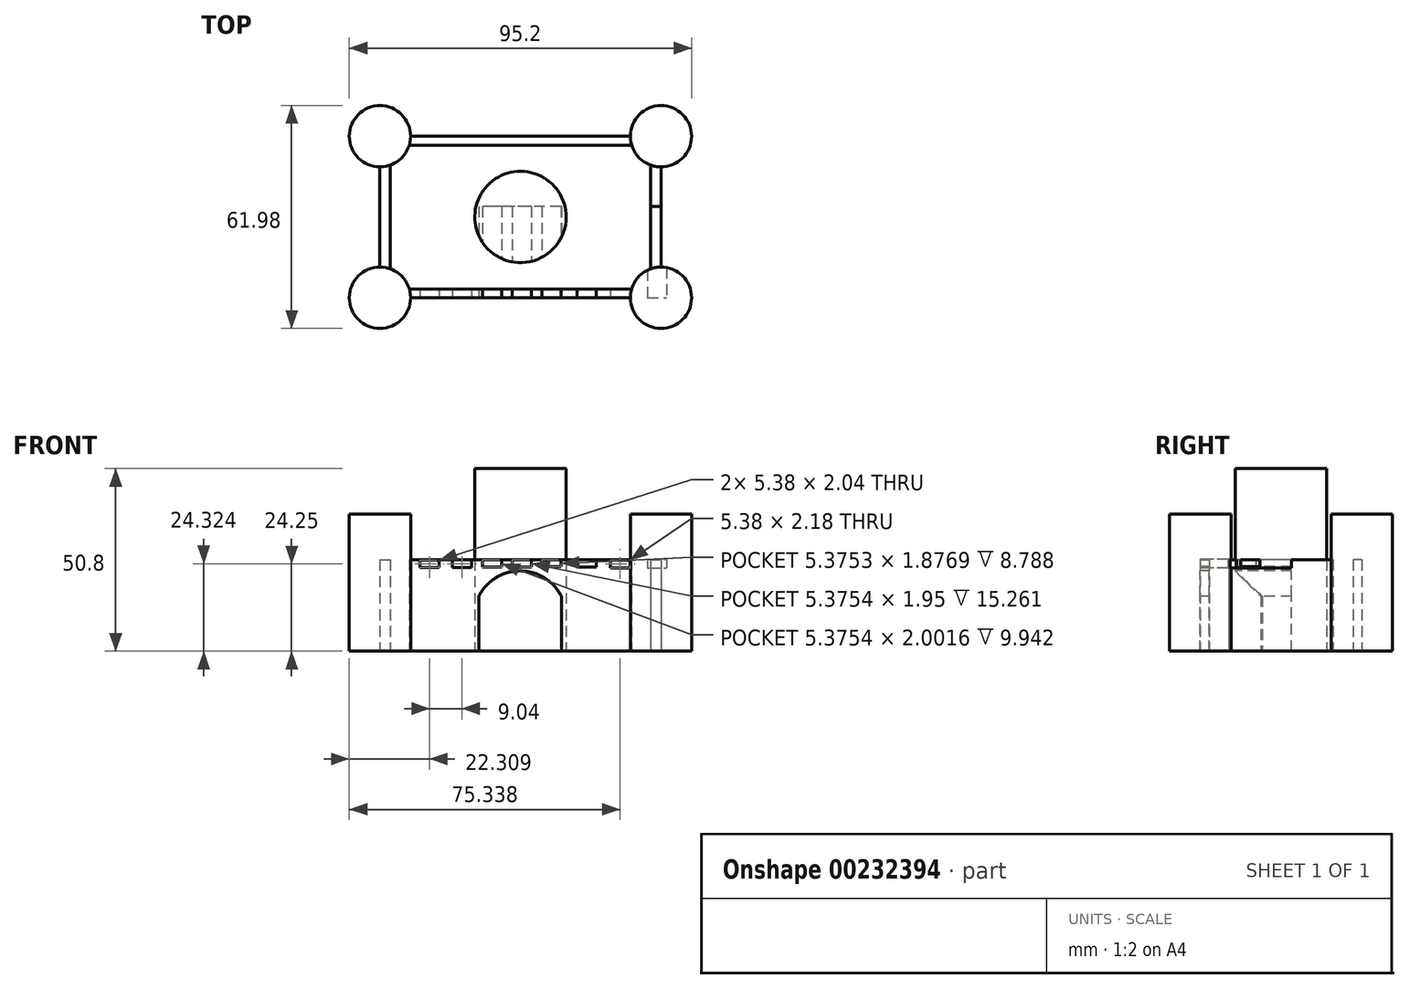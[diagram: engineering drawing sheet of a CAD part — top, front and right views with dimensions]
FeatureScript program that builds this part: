
annotation { "Feature Type Name" : "Feature", "Feature Type Description" : "" }
export const myFeature = defineFeature(function(context is Context, id is Id, definition is map)
    precondition{}
    {
        {
            var Q0;
            Q0=qCreatedBy(makeId("Top.planeOp"),FACE);
            var sketch = newSketch(context, id + "F0", { "sketchPlane" : qUnion([Q0])});
            skLineSegment(sketch, "E0.bottom", {"start": v(30.54, 22.46) * mm, "end": v(-30.54, 22.46) * mm});
            skLineSegment(sketch, "E0.top", {"start": v(30.54, -22.46) * mm, "end": v(-30.54, -22.46) * mm});
            skLineSegment(sketch, "E0.left", {"start": v(39.07, 13.93) * mm, "end": v(39.07, -13.93) * mm});
            skLineSegment(sketch, "E0.right", {"start": v(-39.07, 13.93) * mm, "end": v(-39.07, -13.93) * mm});
            skPoint(sketch, "E0.middle", {"position": v(0, 0) * mm});
            skCircle(sketch, "E1", {"center": v(0, 0) * mm, "radius": 12.7 * mm});
            skCircle(sketch, "E2", {"center": v(-39.07, 22.46) * mm, "radius": 8.53 * mm});
            skCircle(sketch, "E3", {"center": v(39.07, 22.46) * mm, "radius": 8.53 * mm});
            skCircle(sketch, "E4", {"center": v(39.07, -22.46) * mm, "radius": 8.53 * mm});
            skCircle(sketch, "E5", {"center": v(-39.07, -22.46) * mm, "radius": 8.53 * mm});
            skLineSegment(sketch, "E6.bottom", {"start": v(30.9, 20) * mm, "end": v(-30.9, 20) * mm});
            skLineSegment(sketch, "E6.top", {"start": v(30.9, -20) * mm, "end": v(-30.9, -20) * mm});
            skLineSegment(sketch, "E6.left", {"start": v(36.15, 14.45) * mm, "end": v(36.15, -14.45) * mm});
            skLineSegment(sketch, "E6.right", {"start": v(-36.15, 14.45) * mm, "end": v(-36.15, -14.45) * mm});
            skPoint(sketch, "E7.orphan", {"position": v(36.15, 20) * mm});
            skPoint(sketch, "E8.orphan", {"position": v(36.15, -20) * mm});
            skPoint(sketch, "E9.orphan", {"position": v(-36.15, -20) * mm});
            skPoint(sketch, "E10.orphan", {"position": v(-36.15, 20) * mm});
            skSolve(sketch);
        }
        {
            var Q0;
            {var subQ0=sQuery(id+"F0.wireOp",EDGE,"E0.bottom");Q0=makeQuery(id+"F0.imprint","IMPRINT",FACE,{"disambiguationData":[TD([[makeQuery(id+"F0.imprint","IMPRINT",EDGE,{"derivedFrom":subQ0}),1.0]])]});}
            var Q1;
            {var subQ0=sQuery(id+"F0.wireOp",EDGE,"E0.right");Q1=makeQuery(id+"F0.imprint","IMPRINT",FACE,{"disambiguationData":[TD([[makeQuery(id+"F0.imprint","IMPRINT",EDGE,{"derivedFrom":subQ0}),1.0]])]});}
            var Q2;
            {var subQ0=sQuery(id+"F0.wireOp",EDGE,"E0.top");Q2=makeQuery(id+"F0.imprint","IMPRINT",FACE,{"disambiguationData":[TD([[makeQuery(id+"F0.imprint","IMPRINT",EDGE,{"derivedFrom":subQ0}),-1.0]])]});}
            var Q3;
            {var subQ0=sQuery(id+"F0.wireOp",EDGE,"E0.left");Q3=makeQuery(id+"F0.imprint","IMPRINT",FACE,{"disambiguationData":[TD([[makeQuery(id+"F0.imprint","IMPRINT",EDGE,{"derivedFrom":subQ0}),-1.0]])]});}
            extrude(context, id + "F1", {"entities" : qUnion([Q0, Q1, Q2, Q3]), "depth" : 25.4 * mm});
        }
        {
            var Q0;
            {var subQ0=sQuery(id+"F0.wireOp",EDGE,"E3");var subQ1=makeQuery(id+"F0.imprint","INTERSECT",VERTEX,{"derivedFrom":[sQuery(id+"F0.wireOp",EDGE,"E0.bottom"),subQ0]});Q0=makeQuery(id+"F0.imprint","IMPRINT",FACE,{"disambiguationData":[TD([[makeQuery(id+"F0.imprint","IMPRINT",EDGE,{"disambiguationData":[TD([[subQ1,-1.0]])],"derivedFrom":subQ0}),1.0]])]});}
            var Q1;
            {var subQ0=sQuery(id+"F0.wireOp",EDGE,"E4");var subQ1=makeQuery(id+"F0.imprint","INTERSECT",VERTEX,{"derivedFrom":[sQuery(id+"F0.wireOp",EDGE,"E0.left"),subQ0]});Q1=makeQuery(id+"F0.imprint","IMPRINT",FACE,{"disambiguationData":[TD([[makeQuery(id+"F0.imprint","IMPRINT",EDGE,{"disambiguationData":[TD([[subQ1,-1.0]])],"derivedFrom":subQ0}),1.0]])]});}
            var Q2;
            {var subQ0=sQuery(id+"F0.wireOp",EDGE,"E5");var subQ1=makeQuery(id+"F0.imprint","INTERSECT",VERTEX,{"derivedFrom":[sQuery(id+"F0.wireOp",EDGE,"E0.top"),subQ0]});Q2=makeQuery(id+"F0.imprint","IMPRINT",FACE,{"disambiguationData":[TD([[makeQuery(id+"F0.imprint","IMPRINT",EDGE,{"disambiguationData":[TD([[subQ1,-1.0]])],"derivedFrom":subQ0}),1.0]])]});}
            var Q3;
            {var subQ0=sQuery(id+"F0.wireOp",EDGE,"E2");var subQ1=makeQuery(id+"F0.imprint","INTERSECT",VERTEX,{"derivedFrom":[sQuery(id+"F0.wireOp",EDGE,"E0.bottom"),subQ0]});Q3=makeQuery(id+"F0.imprint","IMPRINT",FACE,{"disambiguationData":[TD([[makeQuery(id+"F0.imprint","IMPRINT",EDGE,{"disambiguationData":[TD([[subQ1,-1.0]])],"derivedFrom":subQ0}),1.0]])]});}
            extrude(context, id + "F2", {"entities" : qUnion([Q0, Q1, Q2, Q3]), "depth" : 38.1 * mm});
        }
        {
            var Q0;
            Q0=makeQuery(id+"F0.imprint","IMPRINT",FACE,{"disambiguationData":[TD([[makeQuery(id+"F0.imprint","IMPRINT",EDGE,{"derivedFrom":sQuery(id+"F0.wireOp",EDGE,"E1")}),1.0]])]});
            extrude(context, id + "F3", {"entities" : qUnion([Q0]), "depth" : 50.8 * mm});
        }
        {
            var Q0;
            Q0=makeQuery(id+"F1.opExtrude","SWEPT_FACE",FACE,{"disambiguationData":[OSD([sQuery(id+"F0.wireOp",EDGE,"E0.top")])]});
            var sketch = newSketch(context, id + "F4", { "sketchPlane" : qUnion([Q0])});
            skLineSegment(sketch, "E11.bottom", {"start": v(-11.58, 0) * mm, "end": v(11.37, 0) * mm});
            skLineSegment(sketch, "E11.left", {"start": v(-11.58, 0) * mm, "end": v(-11.58, 15.3) * mm});
            skLineSegment(sketch, "E11.right", {"start": v(11.37, 0) * mm, "end": v(11.37, 15.3) * mm});
            skArc(sketch, "E12", {"start": v(11.37, 15.3) * mm, "mid": v(-0.1, 22.33) * mm, "end": v(-11.58, 15.3) * mm});
            skLineSegment(sketch, "E13.bottom", {"start": v(-37, 25.4) * mm, "end": v(-31.63, 25.4) * mm});
            skLineSegment(sketch, "E13.top", {"start": v(-37, 23.36) * mm, "end": v(-31.63, 23.36) * mm});
            skLineSegment(sketch, "E13.left", {"start": v(-37, 25.4) * mm, "end": v(-37, 23.36) * mm});
            skLineSegment(sketch, "E13.right", {"start": v(-31.63, 25.4) * mm, "end": v(-31.63, 23.36) * mm});
            skLineSegment(sketch, "E14.bottom", {"start": v(-27.98, 25.34) * mm, "end": v(-22.6, 25.34) * mm});
            skLineSegment(sketch, "E14.top", {"start": v(-27.98, 23.3) * mm, "end": v(-22.6, 23.3) * mm});
            skLineSegment(sketch, "E14.left", {"start": v(-27.98, 25.34) * mm, "end": v(-27.98, 23.3) * mm});
            skLineSegment(sketch, "E14.right", {"start": v(-22.6, 25.34) * mm, "end": v(-22.6, 23.3) * mm});
            skLineSegment(sketch, "E15.bottom", {"start": v(-18.94, 25.37) * mm, "end": v(-13.56, 25.37) * mm});
            skLineSegment(sketch, "E15.top", {"start": v(-18.94, 23.33) * mm, "end": v(-13.56, 23.33) * mm});
            skLineSegment(sketch, "E15.left", {"start": v(-18.94, 25.37) * mm, "end": v(-18.94, 23.33) * mm});
            skLineSegment(sketch, "E15.right", {"start": v(-13.56, 25.37) * mm, "end": v(-13.56, 23.33) * mm});
            skLineSegment(sketch, "E16.bottom", {"start": v(-10.6, 25.44) * mm, "end": v(-5.22, 25.44) * mm});
            skLineSegment(sketch, "E16.top", {"start": v(-10.6, 23.4) * mm, "end": v(-5.22, 23.4) * mm});
            skLineSegment(sketch, "E16.left", {"start": v(-10.6, 25.44) * mm, "end": v(-10.6, 23.4) * mm});
            skLineSegment(sketch, "E16.right", {"start": v(-5.22, 25.44) * mm, "end": v(-5.22, 23.4) * mm});
            skLineSegment(sketch, "E17.bottom", {"start": v(-2.29, 25.49) * mm, "end": v(3.09, 25.49) * mm});
            skLineSegment(sketch, "E17.top", {"start": v(-2.29, 23.45) * mm, "end": v(3.09, 23.45) * mm});
            skLineSegment(sketch, "E17.left", {"start": v(-2.29, 25.49) * mm, "end": v(-2.29, 23.45) * mm});
            skLineSegment(sketch, "E17.right", {"start": v(3.09, 25.49) * mm, "end": v(3.09, 23.45) * mm});
            skLineSegment(sketch, "E18.bottom", {"start": v(15.7, 25.49) * mm, "end": v(21.07, 25.49) * mm});
            skLineSegment(sketch, "E18.top", {"start": v(15.7, 23.45) * mm, "end": v(21.07, 23.45) * mm});
            skLineSegment(sketch, "E18.left", {"start": v(15.7, 25.49) * mm, "end": v(15.7, 23.45) * mm});
            skLineSegment(sketch, "E18.right", {"start": v(21.07, 25.49) * mm, "end": v(21.07, 23.45) * mm});
            skLineSegment(sketch, "E19.bottom", {"start": v(5.9, 25.56) * mm, "end": v(11.27, 25.56) * mm});
            skLineSegment(sketch, "E19.top", {"start": v(5.9, 23.52) * mm, "end": v(11.27, 23.52) * mm});
            skLineSegment(sketch, "E19.left", {"start": v(5.9, 25.56) * mm, "end": v(5.9, 23.52) * mm});
            skLineSegment(sketch, "E19.right", {"start": v(11.27, 25.56) * mm, "end": v(11.27, 23.52) * mm});
            skLineSegment(sketch, "E20.bottom", {"start": v(25.05, 25.34) * mm, "end": v(30.43, 25.34) * mm});
            skLineSegment(sketch, "E20.top", {"start": v(25.05, 23.16) * mm, "end": v(30.43, 23.16) * mm});
            skLineSegment(sketch, "E20.left", {"start": v(25.05, 25.34) * mm, "end": v(25.05, 23.16) * mm});
            skLineSegment(sketch, "E20.right", {"start": v(30.43, 25.34) * mm, "end": v(30.43, 23.16) * mm});
            skLineSegment(sketch, "E21.bottom", {"start": v(35.28, 25.56) * mm, "end": v(40.66, 25.56) * mm});
            skLineSegment(sketch, "E21.top", {"start": v(35.28, 23.16) * mm, "end": v(40.66, 23.16) * mm});
            skLineSegment(sketch, "E21.left", {"start": v(35.28, 25.56) * mm, "end": v(35.28, 23.16) * mm});
            skLineSegment(sketch, "E21.right", {"start": v(40.66, 25.56) * mm, "end": v(40.66, 23.16) * mm});
            skSolve(sketch);
        }
        {
            var Q0;
            Q0=makeQuery(id+"F4.imprint","IMPRINT",FACE,{"disambiguationData":[TD([[makeQuery(id+"F4.imprint","IMPRINT",EDGE,{"derivedFrom":sQuery(id+"F4.wireOp",EDGE,"E11.bottom")}),-1.0]])]});
            var Q1;
            Q1=makeQuery(id+"F4.imprint","IMPRINT",FACE,{"disambiguationData":[TD([[makeQuery(id+"F4.imprint","IMPRINT",EDGE,{"derivedFrom":sQuery(id+"F4.wireOp",EDGE,"E13.bottom")}),1.0]])]});
            var Q2;
            Q2=makeQuery(id+"F4.imprint","IMPRINT",FACE,{"disambiguationData":[TD([[makeQuery(id+"F4.imprint","IMPRINT",EDGE,{"derivedFrom":sQuery(id+"F4.wireOp",EDGE,"E14.bottom")}),-1.0]])]});
            var Q3;
            Q3=makeQuery(id+"F4.imprint","IMPRINT",FACE,{"disambiguationData":[TD([[makeQuery(id+"F4.imprint","IMPRINT",EDGE,{"derivedFrom":sQuery(id+"F4.wireOp",EDGE,"E15.bottom")}),-1.0]])]});
            var Q4;
            {var subQ0=sQuery(id+"F4.wireOp",EDGE,"E16.top");Q4=makeQuery(id+"F4.imprint","IMPRINT",FACE,{"disambiguationData":[TD([[makeQuery(id+"F4.imprint","IMPRINT",EDGE,{"derivedFrom":subQ0}),1.0]])]});}
            var Q5;
            {var subQ0=sQuery(id+"F4.wireOp",EDGE,"E17.top");Q5=makeQuery(id+"F4.imprint","IMPRINT",FACE,{"disambiguationData":[TD([[makeQuery(id+"F4.imprint","IMPRINT",EDGE,{"derivedFrom":subQ0}),1.0]])]});}
            var Q6;
            {var subQ0=sQuery(id+"F4.wireOp",EDGE,"E19.top");Q6=makeQuery(id+"F4.imprint","IMPRINT",FACE,{"disambiguationData":[TD([[makeQuery(id+"F4.imprint","IMPRINT",EDGE,{"derivedFrom":subQ0}),1.0]])]});}
            var Q7;
            {var subQ0=sQuery(id+"F4.wireOp",EDGE,"E18.top");Q7=makeQuery(id+"F4.imprint","IMPRINT",FACE,{"disambiguationData":[TD([[makeQuery(id+"F4.imprint","IMPRINT",EDGE,{"derivedFrom":subQ0}),1.0]])]});}
            var Q8;
            Q8=makeQuery(id+"F4.imprint","IMPRINT",FACE,{"disambiguationData":[TD([[makeQuery(id+"F4.imprint","IMPRINT",EDGE,{"derivedFrom":sQuery(id+"F4.wireOp",EDGE,"E20.bottom")}),-1.0]])]});
            var Q9;
            {var subQ0=sQuery(id+"F4.wireOp",EDGE,"E21.top");Q9=makeQuery(id+"F4.imprint","IMPRINT",FACE,{"disambiguationData":[TD([[makeQuery(id+"F4.imprint","IMPRINT",EDGE,{"derivedFrom":subQ0}),1.0]])]});}
            extrude(context, id + "F5", {"entities" : qUnion([Q0, Q1, Q2, Q3, Q4, Q5, Q6, Q7, Q8, Q9]), "operationType" : NewBodyOperationType.REMOVE, "oppositeDirection" : true, "depth" : 25.4 * mm});
        }
    });
